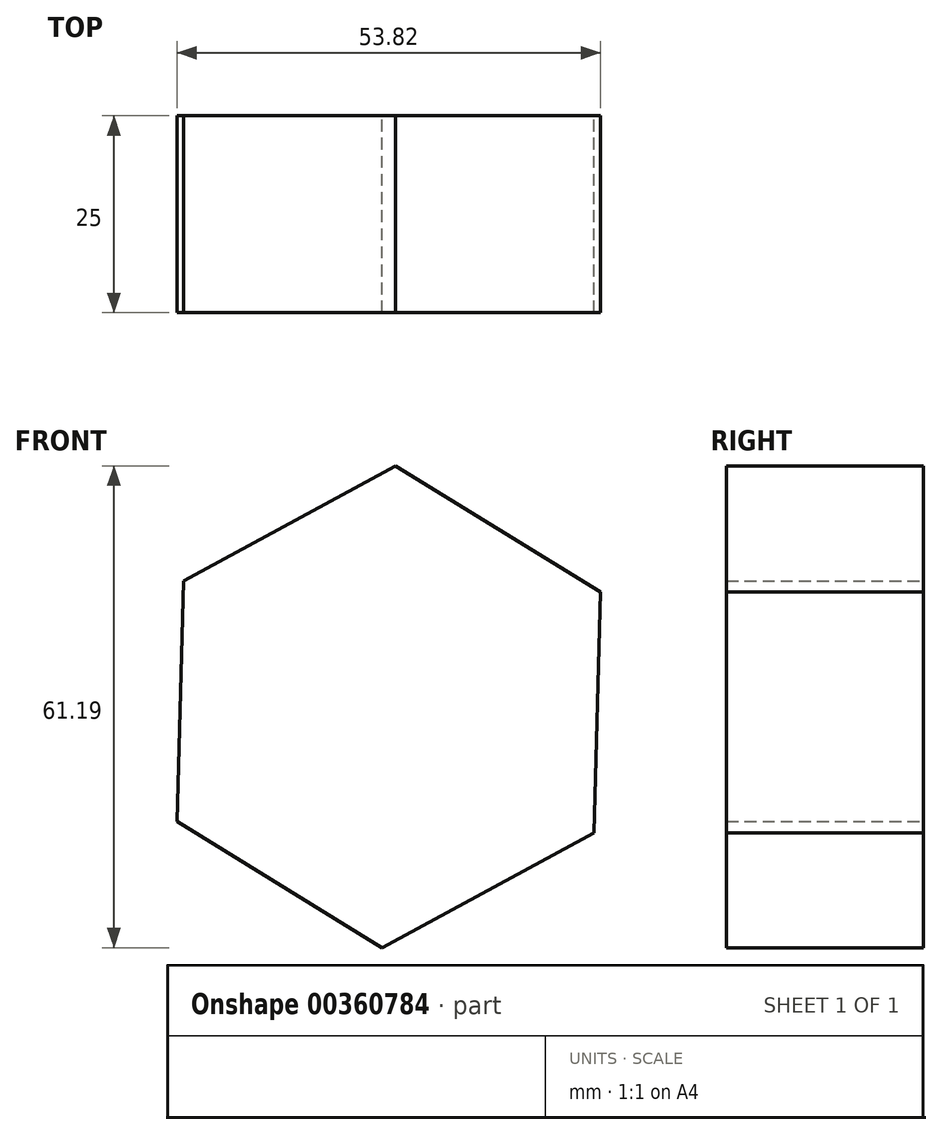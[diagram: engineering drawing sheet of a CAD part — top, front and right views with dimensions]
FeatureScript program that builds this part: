
annotation { "Feature Type Name" : "Feature", "Feature Type Description" : "" }
export const myFeature = defineFeature(function(context is Context, id is Id, definition is map)
    precondition{}
    {
        {
            var Q0;
            Q0=qCreatedBy(makeId("Front.planeOp"),FACE);
            var sketch = newSketch(context, id + "F0", { "sketchPlane" : qUnion([Q0])});
            skCircle(sketch, "E0.cCircle", {"center": v(-145.18, 57.1) * mm, "radius": 26.5 * mm, "construction": true});
            skLineSegment(sketch, "E0.0", {"start": v(-146.02, 26.51) * mm, "end": v(-172.1, 42.53) * mm});
            skLineSegment(sketch, "E0.1", {"start": v(-172.1, 42.53) * mm, "end": v(-171.26, 73.12) * mm});
            skLineSegment(sketch, "E0.2", {"start": v(-171.26, 73.12) * mm, "end": v(-144.35, 87.7) * mm});
            skLineSegment(sketch, "E0.3", {"start": v(-144.35, 87.7) * mm, "end": v(-118.27, 71.68) * mm});
            skLineSegment(sketch, "E0.4", {"start": v(-118.27, 71.68) * mm, "end": v(-119.1, 41.09) * mm});
            skLineSegment(sketch, "E0.5", {"start": v(-119.1, 41.09) * mm, "end": v(-146.02, 26.51) * mm});
            skPoint(sketch, "E0.0.midPoint", {"position": v(-159.05, 34.52) * mm});
            skSolve(sketch);
        }
        {
            var Q0;
            Q0=makeQuery(id+"F0.imprint","IMPRINT",FACE,{"disambiguationData":[TD([[makeQuery(id+"F0.imprint","IMPRINT",EDGE,{"derivedFrom":sQuery(id+"F0.wireOp",EDGE,"E0.0")}),-1.0]])]});
            extrude(context, id + "F1", {"entities" : qUnion([Q0]), "depth" : 25 * mm});
        }
    });
